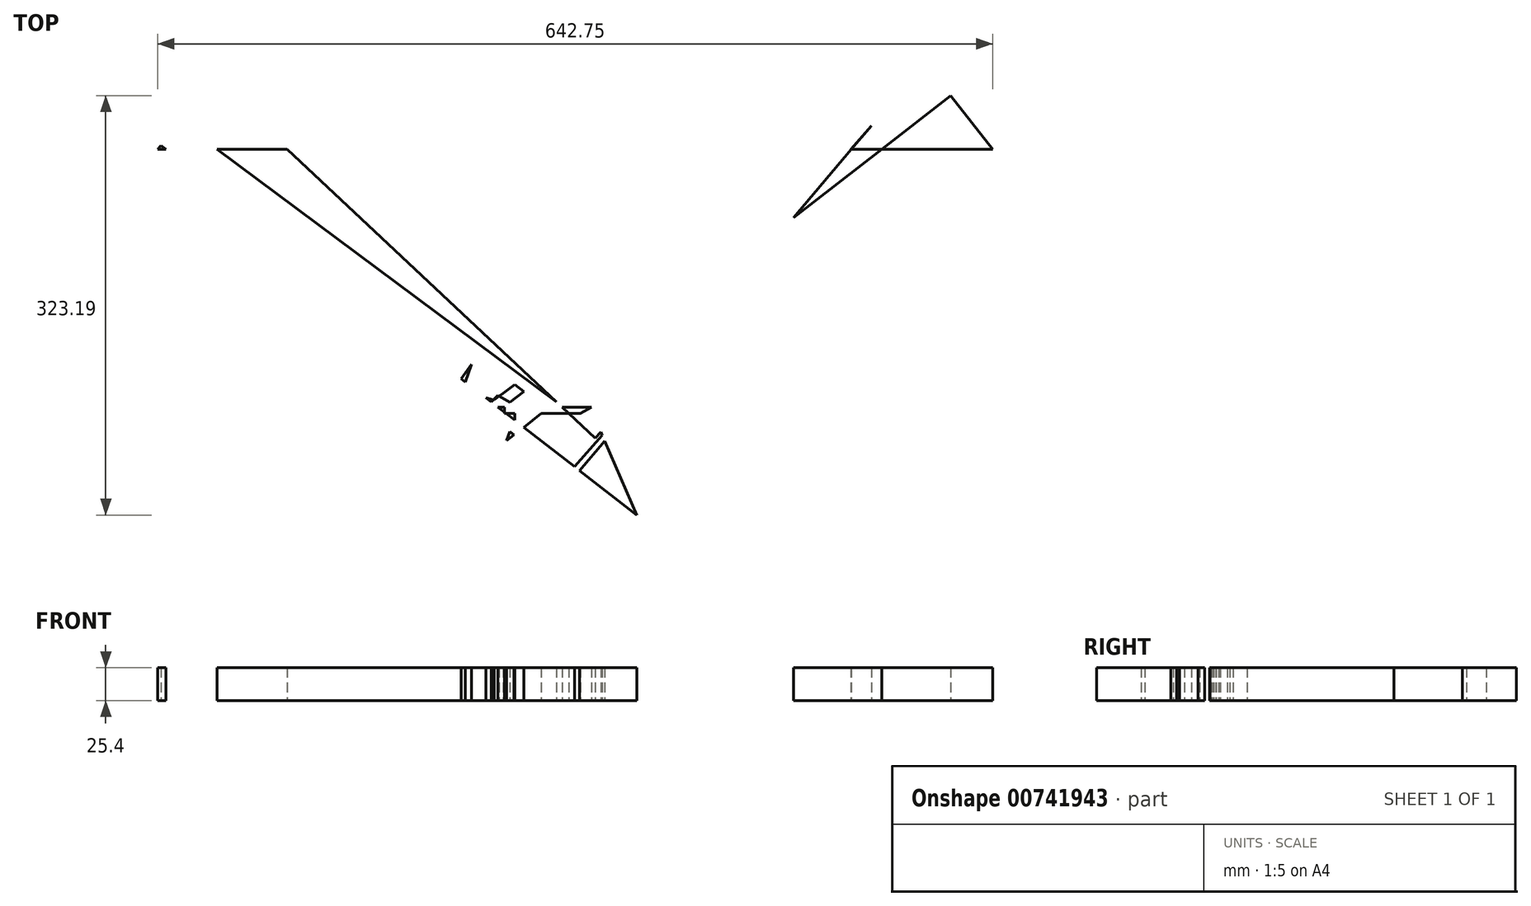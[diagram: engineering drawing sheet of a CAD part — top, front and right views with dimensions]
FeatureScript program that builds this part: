
annotation { "Feature Type Name" : "Feature", "Feature Type Description" : "" }
export const myFeature = defineFeature(function(context is Context, id is Id, definition is map)
    precondition{}
    {
        {
            var Q0;
            Q0=qCreatedBy(makeId("Top.planeOp"),FACE);
            var sketch = newSketch(context, id + "F0", { "sketchPlane" : qUnion([Q0])});
            skLineSegment(sketch, "E0", {"start": v(535.54, 440.62) * mm, "end": v(0, 30.98) * mm});
            skLineSegment(sketch, "E1", {"start": v(535.54, 440.62) * mm, "end": v(535.54, -412.72) * mm});
            skLineSegment(sketch, "E2", {"start": v(535.54, -412.72) * mm, "end": v(-10.63, 0) * mm});
            skLineSegment(sketch, "E3", {"start": v(-10.63, 0) * mm, "end": v(-17.39, -17.18) * mm});
            skLineSegment(sketch, "E4", {"start": v(-17.39, -17.18) * mm, "end": v(-5.53, -52.5) * mm});
            skLineSegment(sketch, "E5", {"start": v(0, -56.69) * mm, "end": v(-5.53, -52.5) * mm});
            skPoint(sketch, "E6", {"position": v(-10.83, 22.7) * mm});
            skLineSegment(sketch, "E7", {"start": v(-10.83, 22.7) * mm, "end": v(-22.9, 29.75) * mm});
            skLineSegment(sketch, "E8", {"start": v(-15.82, 29.75) * mm, "end": v(-22.9, 29.75) * mm});
            skLineSegment(sketch, "E9", {"start": v(-15.82, 29.75) * mm, "end": v(32.52, 190.6) * mm});
            skLineSegment(sketch, "E10", {"start": v(32.52, 190.6) * mm, "end": v(-43.5, 29.75) * mm});
            skLineSegment(sketch, "E11", {"start": v(-43.5, 29.75) * mm, "end": v(-15.82, 22.7) * mm});
            skLineSegment(sketch, "E12", {"start": v(-25.27, 22.7) * mm, "end": v(-15.82, 22.7) * mm});
            skLineSegment(sketch, "E13", {"start": v(-25.27, 22.7) * mm, "end": v(535.54, 440.62) * mm});
            skPoint(sketch, "E14", {"position": v(535.54, 18.87) * mm});
            skLineSegment(sketch, "E15", {"start": v(535.54, 13.95) * mm, "end": v(-43.5, 13.95) * mm});
            skLineSegment(sketch, "E16", {"start": v(-43.5, 13.95) * mm, "end": v(-52.13, 18.87) * mm});
            skLineSegment(sketch, "E17", {"start": v(-52.13, 18.87) * mm, "end": v(-56.32, 29.75) * mm});
            skLineSegment(sketch, "E18", {"start": v(-56.32, 29.75) * mm, "end": v(-40.3, 51.81) * mm});
            skLineSegment(sketch, "E19", {"start": v(-40.3, 51.81) * mm, "end": v(-48.94, 26.87) * mm});
            skLineSegment(sketch, "E20", {"start": v(-48.94, 26.87) * mm, "end": v(-43.5, 18.87) * mm});
            skLineSegment(sketch, "E21", {"start": v(-43.5, 18.87) * mm, "end": v(535.54, 18.87) * mm});
            skPoint(sketch, "E22", {"position": v(535.54, 217.48) * mm});
            skLineSegment(sketch, "E23", {"start": v(535.54, 217.48) * mm, "end": v(182.05, 217.48) * mm});
            skLineSegment(sketch, "E24", {"start": v(182.05, 217.48) * mm, "end": v(-55.01, -5) * mm});
            skLineSegment(sketch, "E25", {"start": v(-55.01, -5) * mm, "end": v(-59.38, -0.34) * mm});
            skLineSegment(sketch, "E26", {"start": v(-59.38, -0.34) * mm, "end": v(-103.31, -101.56) * mm});
            skLineSegment(sketch, "E27", {"start": v(-103.31, -101.56) * mm, "end": v(176.42, -732.82) * mm});
            skLineSegment(sketch, "E28", {"start": v(176.42, -732.82) * mm, "end": v(-55.01, -228.51) * mm});
            skLineSegment(sketch, "E29", {"start": v(182.05, -412.72) * mm, "end": v(-55.01, -228.51) * mm});
            skLineSegment(sketch, "E30", {"start": v(182.05, -412.72) * mm, "end": v(535.54, -412.72) * mm});
            skPoint(sketch, "E31", {"position": v(262.45, -206.36) * mm});
            skLineSegment(sketch, "E32", {"start": v(-328.78, 258.9) * mm, "end": v(535.54, -412.72) * mm});
            skLineSegment(sketch, "E33", {"start": v(-328.78, 258.9) * mm, "end": v(-529.96, 0) * mm});
            skLineSegment(sketch, "E34", {"start": v(-529.96, 0) * mm, "end": v(127.61, 870.2) * mm});
            skLineSegment(sketch, "E35", {"start": v(127.61, 870.2) * mm, "end": v(262.45, 395.14) * mm});
            skLineSegment(sketch, "E36", {"start": v(262.45, 395.14) * mm, "end": v(-328.78, 1270.73) * mm});
            skLineSegment(sketch, "E37", {"start": v(-328.78, 1270.73) * mm, "end": v(262.45, -206.36) * mm});
            skLineSegment(sketch, "E38.MirrorCS", {"start": v(25.27, 22.7) * mm, "end": v(-535.54, 440.62) * mm});
            skLineSegment(sketch, "E39.MirrorCS", {"start": v(-535.54, 440.62) * mm, "end": v(-535.54, -412.72) * mm});
            skLineSegment(sketch, "E40.MirrorCS", {"start": v(43.5, 13.95) * mm, "end": v(52.13, 18.87) * mm});
            skLineSegment(sketch, "E41.MirrorCS", {"start": v(10.83, 22.7) * mm, "end": v(22.9, 29.75) * mm});
            skLineSegment(sketch, "E42.MirrorCS", {"start": v(48.94, 26.87) * mm, "end": v(43.5, 18.87) * mm});
            skLineSegment(sketch, "E43.MirrorCS", {"start": v(328.78, 258.9) * mm, "end": v(529.96, 0) * mm});
            skLineSegment(sketch, "E44.MirrorCS", {"start": v(-535.54, -412.72) * mm, "end": v(10.63, 0) * mm});
            skLineSegment(sketch, "E45.MirrorCS", {"start": v(529.96, 0) * mm, "end": v(-127.61, 870.2) * mm});
            skLineSegment(sketch, "E46.MirrorCS", {"start": v(55.01, -5) * mm, "end": v(59.38, -0.34) * mm});
            skLineSegment(sketch, "E47.MirrorCS", {"start": v(0, -56.69) * mm, "end": v(5.53, -52.5) * mm});
            skPoint(sketch, "E48.MirrorP", {"position": v(10.83, 22.7) * mm});
            skLineSegment(sketch, "E49.MirrorCS", {"start": v(-182.05, -412.72) * mm, "end": v(-535.54, -412.72) * mm});
            skLineSegment(sketch, "E50.MirrorCS", {"start": v(-535.54, 13.95) * mm, "end": v(43.5, 13.95) * mm});
            skLineSegment(sketch, "E51.MirrorCS", {"start": v(56.32, 29.75) * mm, "end": v(40.3, 51.81) * mm});
            skLineSegment(sketch, "E52.MirrorCS", {"start": v(-262.45, 395.14) * mm, "end": v(328.78, 1270.73) * mm});
            skPoint(sketch, "E53.MirrorP", {"position": v(-262.45, -206.36) * mm});
            skLineSegment(sketch, "E54.MirrorCS", {"start": v(15.82, 29.75) * mm, "end": v(22.9, 29.75) * mm});
            skLineSegment(sketch, "E55.MirrorCS", {"start": v(43.5, 18.87) * mm, "end": v(-535.54, 18.87) * mm});
            skLineSegment(sketch, "E56.MirrorCS", {"start": v(59.38, -0.34) * mm, "end": v(103.31, -101.56) * mm});
            skLineSegment(sketch, "E57.MirrorCS", {"start": v(-182.05, -412.72) * mm, "end": v(55.01, -228.51) * mm});
            skLineSegment(sketch, "E58.MirrorCS", {"start": v(17.39, -17.18) * mm, "end": v(5.53, -52.5) * mm});
            skLineSegment(sketch, "E59.MirrorCS", {"start": v(328.78, 258.9) * mm, "end": v(-535.54, -412.72) * mm});
            skLineSegment(sketch, "E60.MirrorCS", {"start": v(-32.52, 190.6) * mm, "end": v(43.5, 29.75) * mm});
            skLineSegment(sketch, "E61.MirrorCS", {"start": v(15.82, 29.75) * mm, "end": v(-32.52, 190.6) * mm});
            skLineSegment(sketch, "E62.MirrorCS", {"start": v(103.31, -101.56) * mm, "end": v(-176.42, -732.82) * mm});
            skLineSegment(sketch, "E63.MirrorCS", {"start": v(-535.54, 440.62) * mm, "end": v(0, 30.98) * mm});
            skLineSegment(sketch, "E64.MirrorCS", {"start": v(52.13, 18.87) * mm, "end": v(56.32, 29.75) * mm});
            skLineSegment(sketch, "E65.MirrorCS", {"start": v(25.27, 22.7) * mm, "end": v(15.82, 22.7) * mm});
            skLineSegment(sketch, "E66.MirrorCS", {"start": v(-535.54, 217.48) * mm, "end": v(-182.05, 217.48) * mm});
            skLineSegment(sketch, "E67.MirrorCS", {"start": v(-176.42, -732.82) * mm, "end": v(55.01, -228.51) * mm});
            skLineSegment(sketch, "E68.MirrorCS", {"start": v(43.5, 29.75) * mm, "end": v(15.82, 22.7) * mm});
            skPoint(sketch, "E69.MirrorP", {"position": v(-535.54, 18.87) * mm});
            skLineSegment(sketch, "E70.MirrorCS", {"start": v(10.63, 0) * mm, "end": v(17.39, -17.18) * mm});
            skLineSegment(sketch, "E71.MirrorCS", {"start": v(-127.61, 870.2) * mm, "end": v(-262.45, 395.14) * mm});
            skPoint(sketch, "E72.MirrorP", {"position": v(-535.54, 217.48) * mm});
            skLineSegment(sketch, "E73.MirrorCS", {"start": v(40.3, 51.81) * mm, "end": v(48.94, 26.87) * mm});
            skLineSegment(sketch, "E74.MirrorCS", {"start": v(328.78, 1270.73) * mm, "end": v(-262.45, -206.36) * mm});
            skLineSegment(sketch, "E75.MirrorCS", {"start": v(-182.05, 217.48) * mm, "end": v(55.01, -5) * mm});
            skPoint(sketch, "E76", {"position": v(267.77, 235.8) * mm});
            skPoint(sketch, "E77", {"position": v(-267.77, 235.8) * mm});
            skLineSegment(sketch, "E78", {"start": v(267.77, 235.8) * mm, "end": v(-14.94, 19.55) * mm});
            skLineSegment(sketch, "E79", {"start": v(-14.94, -89.15) * mm, "end": v(-14.94, 19.55) * mm});
            skLineSegment(sketch, "E80", {"start": v(-14.94, -89.15) * mm, "end": v(267.77, 235.8) * mm});
            skLineSegment(sketch, "E81", {"start": v(-516.33, -89.15) * mm, "end": v(-267.77, 235.8) * mm});
            skPoint(sketch, "E82", {"position": v(-618.55, 504.12) * mm});
            skLineSegment(sketch, "E83", {"start": v(-618.55, 504.12) * mm, "end": v(-516.33, -89.15) * mm});
            skPoint(sketch, "E84", {"position": v(-7.06, 25.58) * mm});
            skPoint(sketch, "E85", {"position": v(7.06, 25.58) * mm});
            skLineSegment(sketch, "E86", {"start": v(7.06, 25.58) * mm, "end": v(7.06, 31.98) * mm});
            skLineSegment(sketch, "E87", {"start": v(7.06, 31.98) * mm, "end": v(-267.77, 235.8) * mm});
            skLineSegment(sketch, "E88", {"start": v(267.77, 235.8) * mm, "end": v(-7.06, -89.15) * mm});
            skLineSegment(sketch, "E89", {"start": v(-7.06, 25.58) * mm, "end": v(-7.06, -89.15) * mm});
            skSolve(sketch);
        }
        {
            var Q0;
            {var subQ2=sQuery(id+"F0.wireOp",EDGE,"E7");Q0=makeQuery(id+"F0.imprint","IMPRINT",FACE,{"disambiguationData":[TD([[makeQuery(id+"F0.imprint","IMPRINT",EDGE,{"derivedFrom":subQ2}),1.0]])]});}
            var Q1;
            {var subQ0=sQuery(id+"F0.wireOp",EDGE,"E15");Q1=makeQuery(id+"F0.imprint","IMPRINT",FACE,{"disambiguationData":[TD([[makeQuery(id+"F0.imprint","IMPRINT",EDGE,{"derivedFrom":subQ0}),-1.0]])]});}
            var Q2;
            {var subQ2=sQuery(id+"F0.wireOp",EDGE,"E23");Q2=makeQuery(id+"F0.imprint","IMPRINT",FACE,{"disambiguationData":[TD([[makeQuery(id+"F0.imprint","IMPRINT",EDGE,{"derivedFrom":subQ2}),1.0]])]});}
            var Q3;
            {var subQ0=sQuery(id+"F0.wireOp",EDGE,"E32");Q3=makeQuery(id+"F0.imprint","IMPRINT",FACE,{"disambiguationData":[TD([[makeQuery(id+"F0.imprint","IMPRINT",EDGE,{"derivedFrom":subQ0}),1.0]])]});}
            var Q4;
            Q4=makeQuery(id+"F0.imprint","IMPRINT",FACE,{"disambiguationData":[TD([[makeQuery(id+"F0.imprint","IMPRINT",EDGE,{"derivedFrom":sQuery(id+"F0.wireOp",EDGE,"E78")}),-1.0]])]});
            var Q5;
            {var subQ2=sQuery(id+"F0.wireOp",EDGE,"E86");Q5=makeQuery(id+"F0.imprint","IMPRINT",FACE,{"disambiguationData":[TD([[makeQuery(id+"F0.imprint","IMPRINT",EDGE,{"derivedFrom":subQ2}),-1.0]])]});}
            var Q6;
            {var subQ11=sQuery(id+"F0.wireOp",EDGE,"E3");Q6=makeQuery(id+"F0.imprint","IMPRINT",FACE,{"disambiguationData":[TD([[makeQuery(id+"F0.imprint","IMPRINT",EDGE,{"derivedFrom":subQ11}),1.0]])]});}
            var Q7;
            {var subQ0=sQuery(id+"F0.wireOp",EDGE,"E88");Q7=makeQuery(id+"F0.imprint","IMPRINT",FACE,{"disambiguationData":[TD([[makeQuery(id+"F0.imprint","IMPRINT",EDGE,{"derivedFrom":subQ0}),-1.0]])]});}
            var Q8;
            {var subQ0=sQuery(id+"F0.wireOp",EDGE,"E81");Q8=makeQuery(id+"F0.imprint","IMPRINT",FACE,{"disambiguationData":[TD([[makeQuery(id+"F0.imprint","IMPRINT",EDGE,{"derivedFrom":subQ0}),-1.0]])]});}
            var Q9;
            {var subQ1=sQuery(id+"F0.wireOp",EDGE,"E38.MirrorCS");Q9=makeQuery(id+"F0.imprint","IMPRINT",FACE,{"disambiguationData":[TD([[makeQuery(id+"F0.imprint","IMPRINT",EDGE,{"derivedFrom":subQ1}),-1.0]])]});}
            var Q10;
            Q10=makeQuery(id+"F0.imprint","IMPRINT",FACE,{"disambiguationData":[TD([[makeQuery(id+"F0.imprint","IMPRINT",EDGE,{"derivedFrom":sQuery(id+"F0.wireOp",EDGE,"E40.MirrorCS")}),1.0]])]});
            var Q11;
            Q11=makeQuery(id+"F0.imprint","IMPRINT",FACE,{"disambiguationData":[TD([[makeQuery(id+"F0.imprint","IMPRINT",EDGE,{"derivedFrom":sQuery(id+"F0.wireOp",EDGE,"E46.MirrorCS")}),-1.0]])]});
            var Q12;
            Q12=makeQuery(id+"F0.imprint","IMPRINT",FACE,{"disambiguationData":[TD([[makeQuery(id+"F0.imprint","IMPRINT",EDGE,{"derivedFrom":sQuery(id+"F0.wireOp",EDGE,"E43.MirrorCS")}),-1.0]])]});
            extrude(context, id + "F1", {"entities" : qUnion([Q0, Q1, Q2, Q3, Q4, Q5, Q6, Q7, Q8, Q9, Q10, Q11, Q12]), "depth" : 25.4 * mm, "offsetDistance" : 25.4 * mm});
        }
        {
            var Q0;
            Q0=qCreatedBy(makeId("Right.planeOp"),FACE);
            var sketch = newSketch(context, id + "F2", { "sketchPlane" : qUnion([Q0])});
            skCircle(sketch, "E90", {"center": v(-35.03, 12.8) * mm, "radius": 6.72 * mm});
            skSolve(sketch);
        }
        {
            var Q0;
            Q0=makeQuery(id+"F2.imprint","IMPRINT",FACE,{"disambiguationData":[TD([[makeQuery(id+"F2.imprint","IMPRINT",EDGE,{"derivedFrom":sQuery(id+"F2.wireOp",EDGE,"E90")}),1.0]])]});
            extrude(context, id + "F3", {"entities" : qUnion([Q0]), "operationType" : NewBodyOperationType.REMOVE, "endBound" : BoundingType.SYMMETRIC, "oppositeDirection" : true, "depth" : 38.6 * mm, "offsetDistance" : 25.4 * mm});
        }
    });
